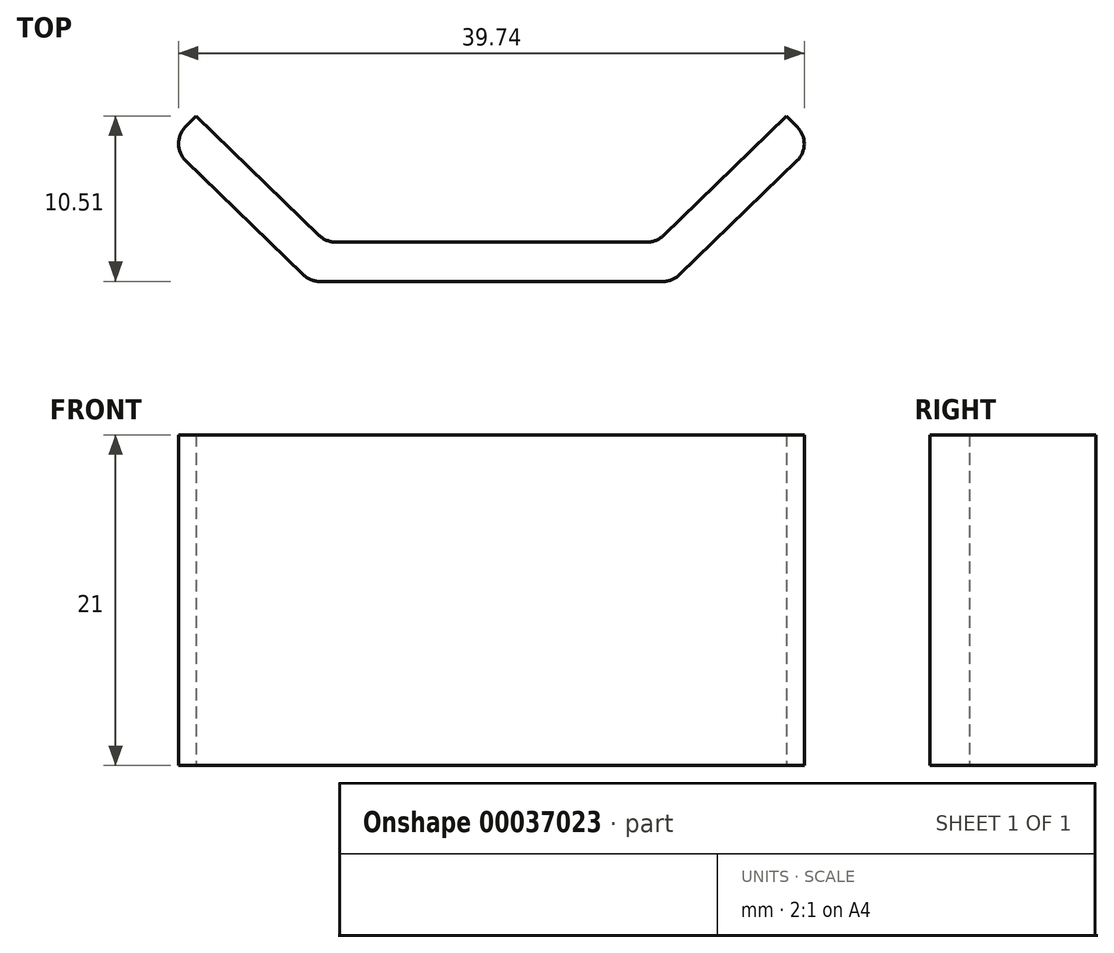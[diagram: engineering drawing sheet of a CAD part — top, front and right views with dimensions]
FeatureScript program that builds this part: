
annotation { "Feature Type Name" : "Feature", "Feature Type Description" : "" }
export const myFeature = defineFeature(function(context is Context, id is Id, definition is map)
    precondition{}
    {
        {
            var Q0;
            Q0=qCreatedBy(makeId("Top.planeOp"),FACE);
            var sketch = newSketch(context, id + "F0", { "sketchPlane" : qUnion([Q0])});
            skLineSegment(sketch, "E0", {"start": v(0, 0) * mm, "end": v(-10.5, 0) * mm});
            skLineSegment(sketch, "E1", {"start": v(-10.5, 0) * mm, "end": v(-18.75, 8.01) * mm});
            skLineSegment(sketch, "E2", {"start": v(-18.75, 8.01) * mm, "end": v(0, 8.01) * mm, "construction": true});
            skLineSegment(sketch, "E3.0", {"start": v(-11.51, -2.5) * mm, "end": v(-20.5, 6.22) * mm});
            skLineSegment(sketch, "E3.1", {"start": v(0, -2.5) * mm, "end": v(-11.51, -2.5) * mm});
            skLineSegment(sketch, "E4", {"start": v(-18.75, 8.01) * mm, "end": v(-20.5, 6.22) * mm});
            skLineSegment(sketch, "E5", {"start": v(0, 8.01) * mm, "end": v(0, -19.22) * mm, "construction": true});
            skLineSegment(sketch, "E6.MirrorCS", {"start": v(0, -2.5) * mm, "end": v(11.51, -2.5) * mm});
            skLineSegment(sketch, "E7.MirrorCS", {"start": v(0, 0) * mm, "end": v(10.5, 0) * mm});
            skLineSegment(sketch, "E8.MirrorCS", {"start": v(11.51, -2.5) * mm, "end": v(20.5, 6.22) * mm});
            skLineSegment(sketch, "E9.MirrorCS", {"start": v(10.5, 0) * mm, "end": v(18.75, 8.01) * mm});
            skLineSegment(sketch, "E10.MirrorCS", {"start": v(18.75, 8.01) * mm, "end": v(20.5, 6.22) * mm});
            skSolve(sketch);
        }
        {
            var Q0;
            Q0 = qSketchRegion(id + "F0", true);
            extrude(context, id + "F1", {"entities" : qUnion([Q0]), "depth" : 21 * mm});
        }
        {
            var Q0;
            Q0=makeQuery(id+"F1.opExtrude","SWEPT_EDGE",EDGE,{"disambiguationData":[OSD([sQuery(id+"F0.wireOp",EDGE,"E0"),sQuery(id+"F0.wireOp",EDGE,"E1")])]});
            var Q1;
            Q1=makeQuery(id+"F1.opExtrude","SWEPT_EDGE",EDGE,{"disambiguationData":[OSD([sQuery(id+"F0.wireOp",EDGE,"E7.MirrorCS"),sQuery(id+"F0.wireOp",EDGE,"E9.MirrorCS")])]});
            var Q2;
            Q2=makeQuery(id+"F1.opExtrude","SWEPT_EDGE",EDGE,{"disambiguationData":[OSD([sQuery(id+"F0.wireOp",EDGE,"E3.0"),sQuery(id+"F0.wireOp",EDGE,"E3.1")])]});
            var Q3;
            Q3=makeQuery(id+"F1.opExtrude","SWEPT_EDGE",EDGE,{"disambiguationData":[OSD([sQuery(id+"F0.wireOp",EDGE,"E6.MirrorCS"),sQuery(id+"F0.wireOp",EDGE,"E8.MirrorCS")])]});
            var Q4;
            Q4=makeQuery(id+"F1.opExtrude","SWEPT_EDGE",EDGE,{"disambiguationData":[OSD([sQuery(id+"F0.wireOp",EDGE,"E3.0"),sQuery(id+"F0.wireOp",EDGE,"E4")])]});
            var Q5;
            Q5=makeQuery(id+"F1.opExtrude","SWEPT_EDGE",EDGE,{"disambiguationData":[OSD([sQuery(id+"F0.wireOp",EDGE,"E8.MirrorCS"),sQuery(id+"F0.wireOp",EDGE,"E10.MirrorCS")])]});
            fillet(context, id + "F2", {"entities" : qUnion([Q0, Q1, Q2, Q3, Q4, Q5]), "radius" : 1.5 * mm, "tangentPropagation" : true, "allowEdgeOverflow" : false});
        }
    });
